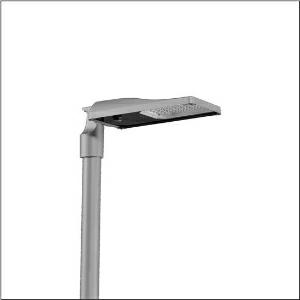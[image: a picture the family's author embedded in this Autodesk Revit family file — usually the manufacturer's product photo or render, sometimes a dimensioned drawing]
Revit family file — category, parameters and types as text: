
# Revit family: streetlight_sl_31_mini___st1_0a_5xh2d3ar08ga_b0cd
name_source: partatom
category: Lighting Fixtures
units: mm (PartAtom-declared; Revit-internal decimal feet)

## family parameters
Cut with Voids When Loaded = No
Host = Face
Light Source = No
Part Type = Normal
Room Calculation Point = No
Round Connector Dimension = Use Diameter
Shared = No

## types (1)
- --- (1 x LED, 5880 lm, 39.3 W, 3000K)
    Apparent Load = 39 VA
    CIE Flux Codes = 37 72 97 100 100
    Color Rendering = 70
    Color Temperature = 3000K
    Default Elevation = 1800 mm
    Description = Streetlight SL 31 mini D4i mast luminaire for post-top, side-entry; light control with lens of PMMA; light distribution: ST1.0a, direct asymmetric distribution, for standard-compliant lighting for roads and squares; LED: luminous flux: 5.880lm, light colour: 730, colour temperature: 3000K; luminous efficacy: 149,6lm/W; control: pre-setting: logarithmic dimming characteristic, flexible luminous flux parameterisation, time-dependent luminous flux control, constant luminous flux control, power reduction, intelligent temperature release in ECG and LED module, overheat protection; luminaire housing, of diecast aluminium, Siteco® metallic grey (DB 702S), corrosivity category C5 high according to DIN EN ISO 12944; cover of toughened safety glass, transparent, mast flange of diecast aluminium, Siteco® metallic grey (DB 702S), spigot size: 76/60mm, mast flange included unmounted; with cable H07RN-F 2x 1.5mm², cable length: 8,5m, connection cable pre-assembled; mains connection: 220..240V, AC, 50/60Hz; power consumption (at start of service life): 39,3W / (at end of service life): 40,7W / (with reduced operation 50%): 18,1W; protection rating (complete): IP66; insulation class (complete): insulation class II (safety insulation); impact resistance: IK09; certification: CE, ENEC, ENEC+, VDE, UKCA, ZD4i; permissible operating ambient temperature for outdoor applications: -40..+50°C; packaging unit: 1 piece

Light Distribution: ST1.0a
    Height = 76 mm
    Lamp = 1 x LED
    Lamp Light Flux = 5880 lm
    Lamp Power = 39.3 W
    Lamp count = 1
    Length = 547 mm
    Luminous efficacy = 150 lm/W
    Manufacturer = Siteco
    ModVariant = No
    Model = 5XH2D3AR08GA
    Number of Poles = 1
    OnlyDefault = Yes
    Power Factor = 1
    Product Name = Streetlight SL 31 mini | ST1.0a
    Product group = mast luminaire | pylon top
    ProductGroupID = 6100
    Protection Class = Protection class II
    Protection Degree = IP 66
    RLX_Detail_Level = 1
    RLX_Emergency_Light_Flux = 0 lm
    RLX_Emergency_Type = 0
    RLX_Emergency_Type_DB = No
    RlxData = <blob elided: 39657 chars, md5=e11fb65c>
    Socket = socket
    Standby Power = 0 W
    System Light Flux = 5880 lm
    System Power = 39 W
    Type Comments = factory setting: luminous flux: 100 % | dim-lin: 254 | 798 mA
    Type Image = l_1300328.jpg
    URL = http://relux.com
    VarID = @adj_054864
    Voltage = 0 V
    Weight = 0.00 kg
    Width = 265 mm

## geometry (parser evidence)
native form markers: Blend x4, Sweep x10
no freeform markers — native parametric forms only
